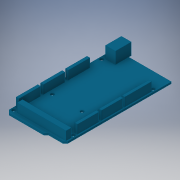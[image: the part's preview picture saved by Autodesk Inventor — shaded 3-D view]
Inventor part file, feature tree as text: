
AUTODESK INVENTOR PART (.ipt)
format: ipt  version: 2018 (Build 220112000, 112)  size: 236,544 bytes
history: native  units: in
note: dims shown in document units (in); Inventor stores cm internally (conversion verified against a paired STEP export)
features: extrude x3, sketch x3, projected_geometry x2
ambient origin geometry x8: Origin, YZ Plane, XZ Plane, XY Plane, X Axis, Y Axis, Z Axis, Center Point
bodies: Solid1 (feature_tree)
feature tree (8):
  extrude  "Extrusion1"  Depth=0.0886in
  extrude  "Extrusion2"  Depth=0.0886in
  extrude  "Extrusion3"  Depth=0.4402in
  sketch  "Sketch1"  dims[d2=0.065in d3=0.0in d4=0.0886in]
  sketch  "Sketch2"  dims[d5=45.0deg d6=0.0886in]
  projected_geometry  "Projected Loop1"
  sketch  "Sketch3"  dims[d7=45.0deg d8=0.1083in d9=1.378in d10=2.0949in d11=4.0in d12=2.0in d13=1.0474in d14=0.1in d15=0.3051in d16=3.25in d17=2.95in d18=1.9in d19=2.6024in d20=0.1252in d21=1.0965in d22=0.5748in d23=1.0in d24=0.8in d25=0.0984in d26=0.8in d27=0.1969in d28=1.8in d29=0.8in d30=0.8in d31=0.8in d32=0.3268in d33=0.0in d34=0.3598in d35=0.4402in d36=0.0in]
  projected_geometry  "Projected Loop2"
